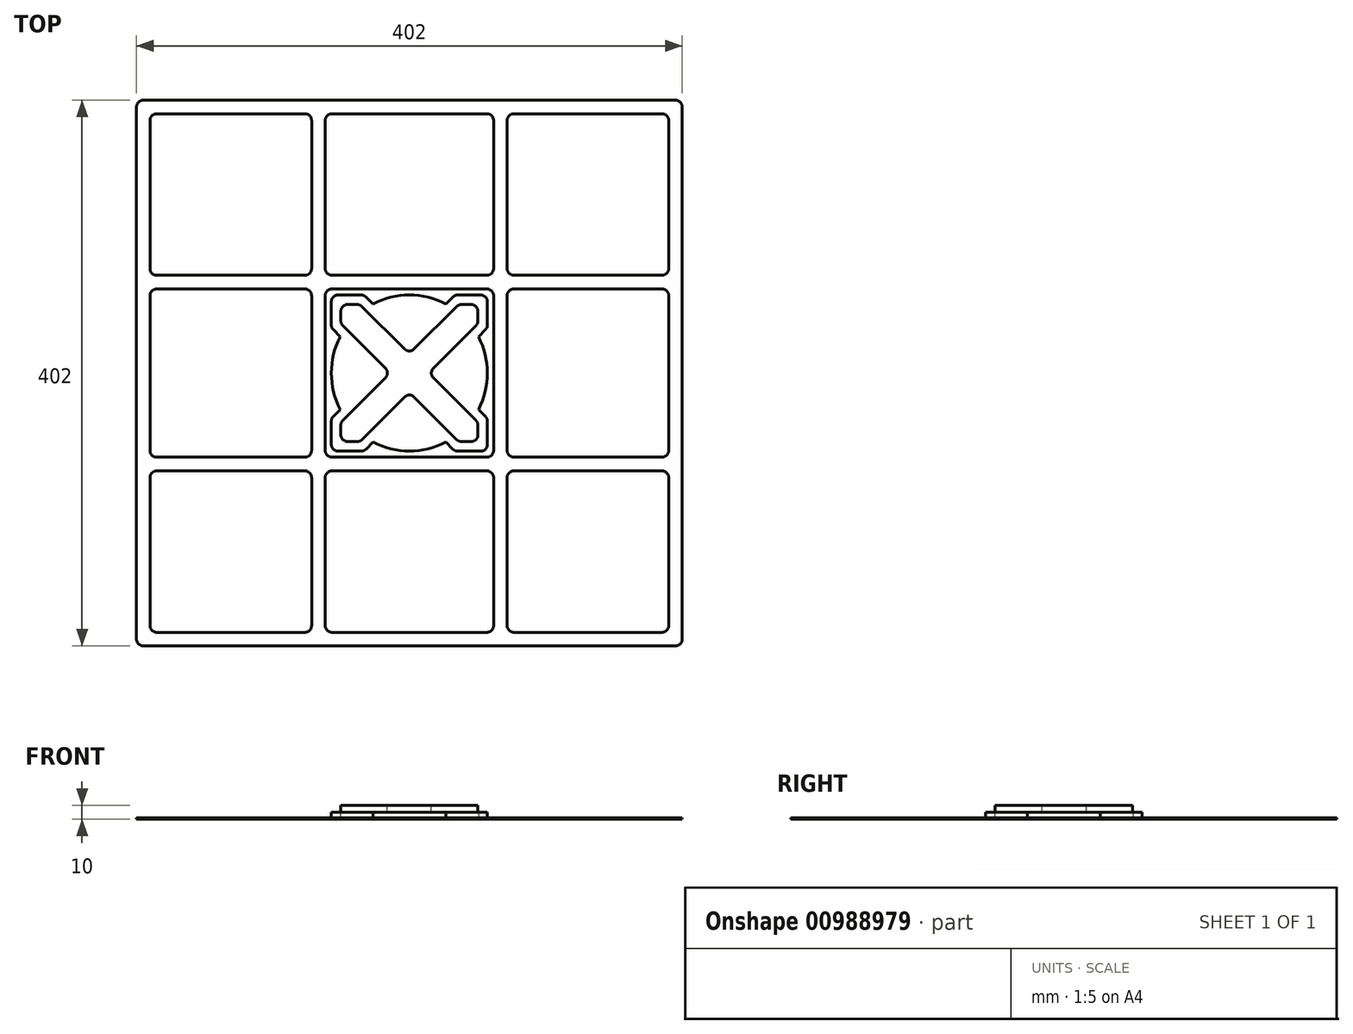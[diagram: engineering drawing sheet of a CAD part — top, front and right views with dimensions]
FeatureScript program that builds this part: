
annotation { "Feature Type Name" : "Feature", "Feature Type Description" : "" }
export const myFeature = defineFeature(function(context is Context, id is Id, definition is map)
    precondition{}
    {
        {
            var Q0;
            Q0=qCreatedBy(makeId("Top.planeOp"),FACE);
            var sketch = newSketch(context, id + "F0", { "sketchPlane" : qUnion([Q0])});
            skLineSegment(sketch, "E0.bottom", {"start": v(57.5, 57.5) * mm, "end": v(-57.5, 57.5) * mm, "construction": true});
            skLineSegment(sketch, "E0.top", {"start": v(57.5, -57.5) * mm, "end": v(-57.5, -57.5) * mm, "construction": true});
            skLineSegment(sketch, "E0.left", {"start": v(57.5, 57.5) * mm, "end": v(57.5, -57.5) * mm, "construction": true});
            skLineSegment(sketch, "E0.right", {"start": v(-57.5, 57.5) * mm, "end": v(-57.5, -57.5) * mm, "construction": true});
            skPoint(sketch, "E0.middle", {"position": v(0, 0) * mm});
            skLineSegment(sketch, "E1", {"start": v(-57.5, 57.5) * mm, "end": v(57.5, -57.5) * mm, "construction": true});
            skLineSegment(sketch, "E2.0", {"start": v(-69.52, 45.48) * mm, "end": v(-24.04, 0) * mm});
            skLineSegment(sketch, "E3.0", {"start": v(-45.48, 69.52) * mm, "end": v(0, 24.04) * mm});
            skLineSegment(sketch, "E4.MirrorCS", {"start": v(45.48, 69.52) * mm, "end": v(0, 24.04) * mm});
            skLineSegment(sketch, "E5.MirrorCS", {"start": v(69.52, 45.48) * mm, "end": v(24.04, 0) * mm});
            skLineSegment(sketch, "E6.trimOffspring", {"start": v(24.04, 0) * mm, "end": v(72.02, -47.98) * mm});
            skLineSegment(sketch, "E7.trimOffspring", {"start": v(-24.04, 0) * mm, "end": v(-72.02, -47.98) * mm});
            skLineSegment(sketch, "E8.trimOffspring", {"start": v(0, -24.04) * mm, "end": v(47.98, -72.02) * mm});
            skLineSegment(sketch, "E9.trimOffspring", {"start": v(0, -24.04) * mm, "end": v(-47.98, -72.02) * mm});
            skLineSegment(sketch, "E10", {"start": v(-57.5, 33.46) * mm, "end": v(-57.5, 57.5) * mm});
            skLineSegment(sketch, "E11", {"start": v(-33.46, 57.5) * mm, "end": v(-57.5, 57.5) * mm});
            skLineSegment(sketch, "E12", {"start": v(33.46, 57.5) * mm, "end": v(57.5, 57.5) * mm});
            skLineSegment(sketch, "E13", {"start": v(57.5, 33.46) * mm, "end": v(57.5, 57.5) * mm});
            skLineSegment(sketch, "E14.MirrorCS", {"start": v(-57.5, -33.46) * mm, "end": v(-57.5, -57.5) * mm});
            skLineSegment(sketch, "E15.MirrorCS", {"start": v(-33.46, -57.5) * mm, "end": v(-57.5, -57.5) * mm});
            skLineSegment(sketch, "E16.MirrorCS", {"start": v(33.46, -57.5) * mm, "end": v(57.5, -57.5) * mm});
            skLineSegment(sketch, "E17.MirrorCS", {"start": v(57.5, -33.46) * mm, "end": v(57.5, -57.5) * mm});
            skSolve(sketch);
        }
        {
            var Q0;
            {var subQ1=sQuery(id+"F0.wireOp",EDGE,"E10");Q0=makeQuery(id+"F0.imprint","IMPRINT",FACE,{"disambiguationData":[TD([[makeQuery(id+"F0.imprint","IMPRINT",EDGE,{"derivedFrom":subQ1}),-1.0]])]});}
            extrude(context, id + "F1", {"entities" : qUnion([Q0]), "depth" : 5 * mm, "offsetDistance" : 25 * mm});
        }
        {
            var Q0;
            Q0=makeQuery(id+"F1.opExtrude","SWEPT_EDGE",EDGE,{"disambiguationData":[OSD([sQuery(id+"F0.wireOp",EDGE,"E14.MirrorCS"),sQuery(id+"F0.wireOp",EDGE,"E15.MirrorCS")])]});
            var Q1;
            Q1=makeQuery(id+"F1.opExtrude","SWEPT_EDGE",EDGE,{"disambiguationData":[OSD([sQuery(id+"F0.wireOp",EDGE,"E9.trimOffspring"),sQuery(id+"F0.wireOp",EDGE,"E15.MirrorCS")])]});
            var Q2;
            Q2=makeQuery(id+"F1.opExtrude","SWEPT_EDGE",EDGE,{"disambiguationData":[OSD([sQuery(id+"F0.wireOp",EDGE,"E8.trimOffspring"),sQuery(id+"F0.wireOp",EDGE,"E16.MirrorCS")])]});
            var Q3;
            Q3=makeQuery(id+"F1.opExtrude","SWEPT_EDGE",EDGE,{"disambiguationData":[OSD([sQuery(id+"F0.wireOp",EDGE,"E8.trimOffspring"),sQuery(id+"F0.wireOp",EDGE,"E9.trimOffspring")])]});
            var Q4;
            Q4=makeQuery(id+"F1.opExtrude","SWEPT_EDGE",EDGE,{"disambiguationData":[OSD([sQuery(id+"F0.wireOp",EDGE,"E16.MirrorCS"),sQuery(id+"F0.wireOp",EDGE,"E17.MirrorCS")])]});
            var Q5;
            Q5=makeQuery(id+"F1.opExtrude","SWEPT_EDGE",EDGE,{"disambiguationData":[OSD([sQuery(id+"F0.wireOp",EDGE,"E6.trimOffspring"),sQuery(id+"F0.wireOp",EDGE,"E17.MirrorCS")])]});
            var Q6;
            Q6=makeQuery(id+"F1.opExtrude","SWEPT_EDGE",EDGE,{"disambiguationData":[OSD([sQuery(id+"F0.wireOp",EDGE,"E5.MirrorCS"),sQuery(id+"F0.wireOp",EDGE,"E6.trimOffspring")])]});
            var Q7;
            Q7=makeQuery(id+"F1.opExtrude","SWEPT_EDGE",EDGE,{"disambiguationData":[OSD([sQuery(id+"F0.wireOp",EDGE,"E5.MirrorCS"),sQuery(id+"F0.wireOp",EDGE,"E13")])]});
            var Q8;
            Q8=makeQuery(id+"F1.opExtrude","SWEPT_EDGE",EDGE,{"disambiguationData":[OSD([sQuery(id+"F0.wireOp",EDGE,"E12"),sQuery(id+"F0.wireOp",EDGE,"E13")])]});
            var Q9;
            Q9=makeQuery(id+"F1.opExtrude","SWEPT_EDGE",EDGE,{"disambiguationData":[OSD([sQuery(id+"F0.wireOp",EDGE,"E4.MirrorCS"),sQuery(id+"F0.wireOp",EDGE,"E12")])]});
            var Q10;
            Q10=makeQuery(id+"F1.opExtrude","SWEPT_EDGE",EDGE,{"disambiguationData":[OSD([sQuery(id+"F0.wireOp",EDGE,"E3.0"),sQuery(id+"F0.wireOp",EDGE,"E4.MirrorCS")])]});
            var Q11;
            Q11=makeQuery(id+"F1.opExtrude","SWEPT_EDGE",EDGE,{"disambiguationData":[OSD([sQuery(id+"F0.wireOp",EDGE,"E3.0"),sQuery(id+"F0.wireOp",EDGE,"E11")])]});
            var Q12;
            Q12=makeQuery(id+"F1.opExtrude","SWEPT_EDGE",EDGE,{"disambiguationData":[OSD([sQuery(id+"F0.wireOp",EDGE,"E10"),sQuery(id+"F0.wireOp",EDGE,"E11")])]});
            var Q13;
            Q13=makeQuery(id+"F1.opExtrude","SWEPT_EDGE",EDGE,{"disambiguationData":[OSD([sQuery(id+"F0.wireOp",EDGE,"E2.0"),sQuery(id+"F0.wireOp",EDGE,"E10")])]});
            var Q14;
            Q14=makeQuery(id+"F1.opExtrude","SWEPT_EDGE",EDGE,{"disambiguationData":[OSD([sQuery(id+"F0.wireOp",EDGE,"E2.0"),sQuery(id+"F0.wireOp",EDGE,"E7.trimOffspring")])]});
            var Q15;
            Q15=makeQuery(id+"F1.opExtrude","SWEPT_EDGE",EDGE,{"disambiguationData":[OSD([sQuery(id+"F0.wireOp",EDGE,"E7.trimOffspring"),sQuery(id+"F0.wireOp",EDGE,"E14.MirrorCS")])]});
            fillet(context, id + "F2", {"entities" : qUnion([Q0, Q1, Q2, Q3, Q4, Q5, Q6, Q7, Q8, Q9, Q10, Q11, Q12, Q13, Q14, Q15]), "radius" : 5 * mm, "tangentPropagation" : true, "allowEdgeOverflow" : false});
        }
        {
            var Q0;
            Q0=qCreatedBy(makeId("Top.planeOp"),FACE);
            var sketch = newSketch(context, id + "F3", { "sketchPlane" : qUnion([Q0])});
            skLineSegment(sketch, "E18.bottom", {"start": v(-57.5, 57.5) * mm, "end": v(57.5, 57.5) * mm, "construction": true});
            skLineSegment(sketch, "E18.top", {"start": v(-57.5, -57.5) * mm, "end": v(57.5, -57.5) * mm, "construction": true});
            skLineSegment(sketch, "E18.left", {"start": v(-57.5, 57.5) * mm, "end": v(-57.5, -57.5) * mm, "construction": true});
            skLineSegment(sketch, "E18.right", {"start": v(57.5, 57.5) * mm, "end": v(57.5, -57.5) * mm, "construction": true});
            skPoint(sketch, "E18.middle", {"position": v(0, 0) * mm});
            skCircle(sketch, "E19", {"center": v(0, 0) * mm, "radius": 57.5 * mm});
            skCircle(sketch, "E20.0", {"center": v(0, 0) * mm, "radius": 22.5 * mm});
            skSolve(sketch);
        }
        {
            var Q0;
            Q0=makeQuery(id+"F3.imprint","IMPRINT",FACE,{"disambiguationData":[TD([[makeQuery(id+"F3.imprint","IMPRINT",EDGE,{"derivedFrom":sQuery(id+"F3.wireOp",EDGE,"E19")}),1.0]])]});
            extrude(context, id + "F4", {"entities" : qUnion([Q0]), "depth" : 5 * mm, "offsetDistance" : 25 * mm});
        }
        {
            var Q0;
            Q0=qCreatedBy(makeId("Top.planeOp"),FACE);
            var sketch = newSketch(context, id + "F5", { "sketchPlane" : qUnion([Q0])});
            skLineSegment(sketch, "E21.bottom", {"start": v(201, 201) * mm, "end": v(-201, 201) * mm});
            skLineSegment(sketch, "E21.top", {"start": v(201, -201) * mm, "end": v(-201, -201) * mm});
            skLineSegment(sketch, "E21.left", {"start": v(201, 201) * mm, "end": v(201, -201) * mm});
            skLineSegment(sketch, "E21.right", {"start": v(-201, 201) * mm, "end": v(-201, -201) * mm});
            skPoint(sketch, "E21.middle", {"position": v(0, 0) * mm});
            skLineSegment(sketch, "E22", {"start": v(-67, 201) * mm, "end": v(-67, -201) * mm, "construction": true});
            skLineSegment(sketch, "E23", {"start": v(201, 67) * mm, "end": v(-201, 67) * mm, "construction": true});
            skLineSegment(sketch, "E24.MirrorCS", {"start": v(67, 201) * mm, "end": v(67, -201) * mm, "construction": true});
            skLineSegment(sketch, "E25.MirrorCS", {"start": v(201, -67) * mm, "end": v(-201, -67) * mm, "construction": true});
            skLineSegment(sketch, "E26.0", {"start": v(-191, 191) * mm, "end": v(-191, 72) * mm});
            skLineSegment(sketch, "E26.1", {"start": v(191, 191) * mm, "end": v(72, 191) * mm});
            skLineSegment(sketch, "E26.2", {"start": v(191, 191) * mm, "end": v(191, 72) * mm});
            skLineSegment(sketch, "E26.3", {"start": v(191, -191) * mm, "end": v(72, -191) * mm});
            skLineSegment(sketch, "E27.0", {"start": v(-72, 191) * mm, "end": v(-72, 72) * mm});
            skLineSegment(sketch, "E28.0", {"start": v(-62, 191) * mm, "end": v(-62, 72) * mm});
            skLineSegment(sketch, "E29.0", {"start": v(191, 72) * mm, "end": v(72, 72) * mm});
            skLineSegment(sketch, "E30.0", {"start": v(191, 62) * mm, "end": v(72, 62) * mm});
            skLineSegment(sketch, "E31.0", {"start": v(62, 191) * mm, "end": v(62, 72) * mm});
            skLineSegment(sketch, "E32.0", {"start": v(72, 191) * mm, "end": v(72, 72) * mm});
            skLineSegment(sketch, "E33.0", {"start": v(191, -62) * mm, "end": v(72, -62) * mm});
            skLineSegment(sketch, "E34.0", {"start": v(191, -72) * mm, "end": v(72, -72) * mm});
            skLineSegment(sketch, "E35.trimOffspring", {"start": v(-191, 62) * mm, "end": v(-191, -62) * mm});
            skLineSegment(sketch, "E36.trimOffspring", {"start": v(-72, 72) * mm, "end": v(-191, 72) * mm});
            skLineSegment(sketch, "E37.trimOffspring", {"start": v(-72, 62) * mm, "end": v(-72, -62) * mm});
            skLineSegment(sketch, "E38.trimOffspring", {"start": v(-72, 62) * mm, "end": v(-191, 62) * mm});
            skLineSegment(sketch, "E39.trimOffspring", {"start": v(-62, 62) * mm, "end": v(-62, -62) * mm});
            skLineSegment(sketch, "E40.trimOffspring", {"start": v(62, 62) * mm, "end": v(62, -62) * mm});
            skLineSegment(sketch, "E41.trimOffspring", {"start": v(62, 72) * mm, "end": v(-62, 72) * mm});
            skLineSegment(sketch, "E42.trimOffspring", {"start": v(72, 62) * mm, "end": v(72, -62) * mm});
            skLineSegment(sketch, "E43.trimOffspring", {"start": v(62, 62) * mm, "end": v(-62, 62) * mm});
            skLineSegment(sketch, "E44.trimOffspring", {"start": v(191, 62) * mm, "end": v(191, -62) * mm});
            skLineSegment(sketch, "E45.trimOffspring", {"start": v(191, -72) * mm, "end": v(191, -191) * mm});
            skLineSegment(sketch, "E46.trimOffspring", {"start": v(62, -72) * mm, "end": v(62, -191) * mm});
            skLineSegment(sketch, "E47.trimOffspring", {"start": v(62, -72) * mm, "end": v(-62, -72) * mm});
            skLineSegment(sketch, "E48.trimOffspring", {"start": v(72, -72) * mm, "end": v(72, -191) * mm});
            skLineSegment(sketch, "E49.trimOffspring", {"start": v(62, -62) * mm, "end": v(-62, -62) * mm});
            skLineSegment(sketch, "E50.trimOffspring", {"start": v(-72, -62) * mm, "end": v(-191, -62) * mm});
            skLineSegment(sketch, "E51.trimOffspring", {"start": v(-72, -72) * mm, "end": v(-72, -191) * mm});
            skLineSegment(sketch, "E52.trimOffspring", {"start": v(-72, -72) * mm, "end": v(-191, -72) * mm});
            skLineSegment(sketch, "E53.trimOffspring", {"start": v(-62, -72) * mm, "end": v(-62, -191) * mm});
            skLineSegment(sketch, "E54.trimOffspring", {"start": v(-72, -191) * mm, "end": v(-191, -191) * mm});
            skLineSegment(sketch, "E55.trimOffspring", {"start": v(62, -191) * mm, "end": v(-62, -191) * mm});
            skLineSegment(sketch, "E56.trimOffspring", {"start": v(-191, -72) * mm, "end": v(-191, -191) * mm});
            skLineSegment(sketch, "E57.trimOffspring", {"start": v(62, 191) * mm, "end": v(-62, 191) * mm});
            skLineSegment(sketch, "E58.trimOffspring", {"start": v(-72, 191) * mm, "end": v(-191, 191) * mm});
            skSolve(sketch);
        }
        {
            var Q0;
            Q0=makeQuery(id+"F5.imprint","IMPRINT",FACE,{"disambiguationData":[TD([[makeQuery(id+"F5.imprint","IMPRINT",EDGE,{"derivedFrom":sQuery(id+"F5.wireOp",EDGE,"E21.bottom")}),1.0]])]});
            extrude(context, id + "F6", {"entities" : qUnion([Q0]), "depth" : 1 * mm, "offsetDistance" : 25 * mm});
        }
        {
            var Q0;
            Q0=makeQuery(id+"F5.imprint","IMPRINT",FACE,{"disambiguationData":[TD([[makeQuery(id+"F5.imprint","IMPRINT",EDGE,{"derivedFrom":sQuery(id+"F5.wireOp",EDGE,"E26.3")}),-1.0]])]});
            var Q1;
            Q1=makeQuery(id+"F5.imprint","IMPRINT",FACE,{"disambiguationData":[TD([[makeQuery(id+"F5.imprint","IMPRINT",EDGE,{"derivedFrom":sQuery(id+"F5.wireOp",EDGE,"E46.trimOffspring")}),-1.0]])]});
            var Q2;
            Q2=makeQuery(id+"F5.imprint","IMPRINT",FACE,{"disambiguationData":[TD([[makeQuery(id+"F5.imprint","IMPRINT",EDGE,{"derivedFrom":sQuery(id+"F5.wireOp",EDGE,"E30.0")}),1.0]])]});
            var Q3;
            Q3=makeQuery(id+"F5.imprint","IMPRINT",FACE,{"disambiguationData":[TD([[makeQuery(id+"F5.imprint","IMPRINT",EDGE,{"derivedFrom":sQuery(id+"F5.wireOp",EDGE,"E51.trimOffspring")}),-1.0]])]});
            var Q4;
            Q4=makeQuery(id+"F5.imprint","IMPRINT",FACE,{"disambiguationData":[TD([[makeQuery(id+"F5.imprint","IMPRINT",EDGE,{"derivedFrom":sQuery(id+"F5.wireOp",EDGE,"E21.bottom")}),1.0]])]});
            var Q5;
            Q5=makeQuery(id+"F5.imprint","IMPRINT",FACE,{"disambiguationData":[TD([[makeQuery(id+"F5.imprint","IMPRINT",EDGE,{"derivedFrom":sQuery(id+"F5.wireOp",EDGE,"E39.trimOffspring")}),1.0]])]});
            var Q6;
            Q6=makeQuery(id+"F5.imprint","IMPRINT",FACE,{"disambiguationData":[TD([[makeQuery(id+"F5.imprint","IMPRINT",EDGE,{"derivedFrom":sQuery(id+"F5.wireOp",EDGE,"E26.0")}),1.0]])]});
            var Q7;
            Q7=makeQuery(id+"F5.imprint","IMPRINT",FACE,{"disambiguationData":[TD([[makeQuery(id+"F5.imprint","IMPRINT",EDGE,{"derivedFrom":sQuery(id+"F5.wireOp",EDGE,"E26.1")}),1.0]])]});
            var Q8;
            Q8=makeQuery(id+"F5.imprint","IMPRINT",FACE,{"disambiguationData":[TD([[makeQuery(id+"F5.imprint","IMPRINT",EDGE,{"derivedFrom":sQuery(id+"F5.wireOp",EDGE,"E35.trimOffspring")}),1.0]])]});
            var Q9;
            Q9=makeQuery(id+"F5.imprint","IMPRINT",FACE,{"disambiguationData":[TD([[makeQuery(id+"F5.imprint","IMPRINT",EDGE,{"derivedFrom":sQuery(id+"F5.wireOp",EDGE,"E28.0")}),1.0]])]});
            extrude(context, id + "F7", {"entities" : qUnion([Q0, Q1, Q2, Q3, Q4, Q5, Q6, Q7, Q8, Q9]), "operationType" : NewBodyOperationType.ADD, "depth" : 0.5 * mm, "offsetDistance" : 25 * mm});
        }
        {
            var Q0;
            Q0=makeQuery(id+"F6.opExtrude","SWEPT_EDGE",EDGE,{"disambiguationData":[OSD([sQuery(id+"F5.wireOp",EDGE,"E31.0"),sQuery(id+"F5.wireOp",EDGE,"E57.trimOffspring")])]});
            var Q1;
            Q1=makeQuery(id+"F6.opExtrude","SWEPT_EDGE",EDGE,{"disambiguationData":[OSD([sQuery(id+"F5.wireOp",EDGE,"E26.1"),sQuery(id+"F5.wireOp",EDGE,"E26.2")])]});
            var Q2;
            Q2=makeQuery(id+"F6.opExtrude","SWEPT_EDGE",EDGE,{"disambiguationData":[OSD([sQuery(id+"F5.wireOp",EDGE,"E27.0"),sQuery(id+"F5.wireOp",EDGE,"E58.trimOffspring")])]});
            var Q3;
            Q3=makeQuery(id+"F6.opExtrude","SWEPT_EDGE",EDGE,{"disambiguationData":[OSD([sQuery(id+"F5.wireOp",EDGE,"E37.trimOffspring"),sQuery(id+"F5.wireOp",EDGE,"E38.trimOffspring")])]});
            var Q4;
            Q4=makeQuery(id+"F6.opExtrude","SWEPT_EDGE",EDGE,{"disambiguationData":[OSD([sQuery(id+"F5.wireOp",EDGE,"E40.trimOffspring"),sQuery(id+"F5.wireOp",EDGE,"E43.trimOffspring")])]});
            var Q5;
            Q5=makeQuery(id+"F6.opExtrude","SWEPT_EDGE",EDGE,{"disambiguationData":[OSD([sQuery(id+"F5.wireOp",EDGE,"E30.0"),sQuery(id+"F5.wireOp",EDGE,"E44.trimOffspring")])]});
            var Q6;
            Q6=makeQuery(id+"F6.opExtrude","SWEPT_EDGE",EDGE,{"disambiguationData":[OSD([sQuery(id+"F5.wireOp",EDGE,"E34.0"),sQuery(id+"F5.wireOp",EDGE,"E45.trimOffspring")])]});
            var Q7;
            Q7=makeQuery(id+"F6.opExtrude","SWEPT_EDGE",EDGE,{"disambiguationData":[OSD([sQuery(id+"F5.wireOp",EDGE,"E46.trimOffspring"),sQuery(id+"F5.wireOp",EDGE,"E47.trimOffspring")])]});
            var Q8;
            Q8=makeQuery(id+"F6.opExtrude","SWEPT_EDGE",EDGE,{"disambiguationData":[OSD([sQuery(id+"F5.wireOp",EDGE,"E51.trimOffspring"),sQuery(id+"F5.wireOp",EDGE,"E52.trimOffspring")])]});
            var Q9;
            Q9=makeQuery(id+"F6.opExtrude","SWEPT_EDGE",EDGE,{"disambiguationData":[OSD([sQuery(id+"F5.wireOp",EDGE,"E26.3"),sQuery(id+"F5.wireOp",EDGE,"E45.trimOffspring")])]});
            var Q10;
            Q10=makeQuery(id+"F6.opExtrude","SWEPT_EDGE",EDGE,{"disambiguationData":[OSD([sQuery(id+"F5.wireOp",EDGE,"E33.0"),sQuery(id+"F5.wireOp",EDGE,"E44.trimOffspring")])]});
            var Q11;
            Q11=makeQuery(id+"F6.opExtrude","SWEPT_EDGE",EDGE,{"disambiguationData":[OSD([sQuery(id+"F5.wireOp",EDGE,"E26.2"),sQuery(id+"F5.wireOp",EDGE,"E29.0")])]});
            var Q12;
            Q12=makeQuery(id+"F6.opExtrude","SWEPT_EDGE",EDGE,{"disambiguationData":[OSD([sQuery(id+"F5.wireOp",EDGE,"E31.0"),sQuery(id+"F5.wireOp",EDGE,"E41.trimOffspring")])]});
            var Q13;
            Q13=makeQuery(id+"F6.opExtrude","SWEPT_EDGE",EDGE,{"disambiguationData":[OSD([sQuery(id+"F5.wireOp",EDGE,"E40.trimOffspring"),sQuery(id+"F5.wireOp",EDGE,"E49.trimOffspring")])]});
            var Q14;
            Q14=makeQuery(id+"F6.opExtrude","SWEPT_EDGE",EDGE,{"disambiguationData":[OSD([sQuery(id+"F5.wireOp",EDGE,"E46.trimOffspring"),sQuery(id+"F5.wireOp",EDGE,"E55.trimOffspring")])]});
            var Q15;
            Q15=makeQuery(id+"F6.opExtrude","SWEPT_EDGE",EDGE,{"disambiguationData":[OSD([sQuery(id+"F5.wireOp",EDGE,"E51.trimOffspring"),sQuery(id+"F5.wireOp",EDGE,"E54.trimOffspring")])]});
            var Q16;
            Q16=makeQuery(id+"F6.opExtrude","SWEPT_EDGE",EDGE,{"disambiguationData":[OSD([sQuery(id+"F5.wireOp",EDGE,"E37.trimOffspring"),sQuery(id+"F5.wireOp",EDGE,"E50.trimOffspring")])]});
            var Q17;
            Q17=makeQuery(id+"F6.opExtrude","SWEPT_EDGE",EDGE,{"disambiguationData":[OSD([sQuery(id+"F5.wireOp",EDGE,"E27.0"),sQuery(id+"F5.wireOp",EDGE,"E36.trimOffspring")])]});
            var Q18;
            Q18=makeQuery(id+"F6.opExtrude","SWEPT_EDGE",EDGE,{"disambiguationData":[OSD([sQuery(id+"F5.wireOp",EDGE,"E26.3"),sQuery(id+"F5.wireOp",EDGE,"E48.trimOffspring")])]});
            var Q19;
            Q19=makeQuery(id+"F6.opExtrude","SWEPT_EDGE",EDGE,{"disambiguationData":[OSD([sQuery(id+"F5.wireOp",EDGE,"E53.trimOffspring"),sQuery(id+"F5.wireOp",EDGE,"E55.trimOffspring")])]});
            var Q20;
            Q20=makeQuery(id+"F6.opExtrude","SWEPT_EDGE",EDGE,{"disambiguationData":[OSD([sQuery(id+"F5.wireOp",EDGE,"E54.trimOffspring"),sQuery(id+"F5.wireOp",EDGE,"E56.trimOffspring")])]});
            var Q21;
            Q21=makeQuery(id+"F6.opExtrude","SWEPT_EDGE",EDGE,{"disambiguationData":[OSD([sQuery(id+"F5.wireOp",EDGE,"E35.trimOffspring"),sQuery(id+"F5.wireOp",EDGE,"E50.trimOffspring")])]});
            var Q22;
            Q22=makeQuery(id+"F6.opExtrude","SWEPT_EDGE",EDGE,{"disambiguationData":[OSD([sQuery(id+"F5.wireOp",EDGE,"E39.trimOffspring"),sQuery(id+"F5.wireOp",EDGE,"E49.trimOffspring")])]});
            var Q23;
            Q23=makeQuery(id+"F6.opExtrude","SWEPT_EDGE",EDGE,{"disambiguationData":[OSD([sQuery(id+"F5.wireOp",EDGE,"E33.0"),sQuery(id+"F5.wireOp",EDGE,"E42.trimOffspring")])]});
            var Q24;
            Q24=makeQuery(id+"F6.opExtrude","SWEPT_EDGE",EDGE,{"disambiguationData":[OSD([sQuery(id+"F5.wireOp",EDGE,"E29.0"),sQuery(id+"F5.wireOp",EDGE,"E32.0")])]});
            var Q25;
            Q25=makeQuery(id+"F6.opExtrude","SWEPT_EDGE",EDGE,{"disambiguationData":[OSD([sQuery(id+"F5.wireOp",EDGE,"E28.0"),sQuery(id+"F5.wireOp",EDGE,"E41.trimOffspring")])]});
            var Q26;
            Q26=makeQuery(id+"F6.opExtrude","SWEPT_EDGE",EDGE,{"disambiguationData":[OSD([sQuery(id+"F5.wireOp",EDGE,"E26.0"),sQuery(id+"F5.wireOp",EDGE,"E36.trimOffspring")])]});
            var Q27;
            Q27=makeQuery(id+"F6.opExtrude","SWEPT_EDGE",EDGE,{"disambiguationData":[OSD([sQuery(id+"F5.wireOp",EDGE,"E26.0"),sQuery(id+"F5.wireOp",EDGE,"E58.trimOffspring")])]});
            var Q28;
            Q28=makeQuery(id+"F6.opExtrude","SWEPT_EDGE",EDGE,{"disambiguationData":[OSD([sQuery(id+"F5.wireOp",EDGE,"E28.0"),sQuery(id+"F5.wireOp",EDGE,"E57.trimOffspring")])]});
            var Q29;
            Q29=makeQuery(id+"F6.opExtrude","SWEPT_EDGE",EDGE,{"disambiguationData":[OSD([sQuery(id+"F5.wireOp",EDGE,"E26.1"),sQuery(id+"F5.wireOp",EDGE,"E32.0")])]});
            var Q30;
            Q30=makeQuery(id+"F6.opExtrude","SWEPT_EDGE",EDGE,{"disambiguationData":[OSD([sQuery(id+"F5.wireOp",EDGE,"E30.0"),sQuery(id+"F5.wireOp",EDGE,"E42.trimOffspring")])]});
            var Q31;
            Q31=makeQuery(id+"F6.opExtrude","SWEPT_EDGE",EDGE,{"disambiguationData":[OSD([sQuery(id+"F5.wireOp",EDGE,"E39.trimOffspring"),sQuery(id+"F5.wireOp",EDGE,"E43.trimOffspring")])]});
            var Q32;
            Q32=makeQuery(id+"F6.opExtrude","SWEPT_EDGE",EDGE,{"disambiguationData":[OSD([sQuery(id+"F5.wireOp",EDGE,"E35.trimOffspring"),sQuery(id+"F5.wireOp",EDGE,"E38.trimOffspring")])]});
            var Q33;
            Q33=makeQuery(id+"F6.opExtrude","SWEPT_EDGE",EDGE,{"disambiguationData":[OSD([sQuery(id+"F5.wireOp",EDGE,"E52.trimOffspring"),sQuery(id+"F5.wireOp",EDGE,"E56.trimOffspring")])]});
            var Q34;
            Q34=makeQuery(id+"F6.opExtrude","SWEPT_EDGE",EDGE,{"disambiguationData":[OSD([sQuery(id+"F5.wireOp",EDGE,"E47.trimOffspring"),sQuery(id+"F5.wireOp",EDGE,"E53.trimOffspring")])]});
            var Q35;
            Q35=makeQuery(id+"F6.opExtrude","SWEPT_EDGE",EDGE,{"disambiguationData":[OSD([sQuery(id+"F5.wireOp",EDGE,"E34.0"),sQuery(id+"F5.wireOp",EDGE,"E48.trimOffspring")])]});
            fillet(context, id + "F8", {"entities" : qUnion([Q0, Q1, Q2, Q3, Q4, Q5, Q6, Q7, Q8, Q9, Q10, Q11, Q12, Q13, Q14, Q15, Q16, Q17, Q18, Q19, Q20, Q21, Q22, Q23, Q24, Q25, Q26, Q27, Q28, Q29, Q30, Q31, Q32, Q33, Q34, Q35]), "radius" : 5 * mm, "tangentPropagation" : true, "allowEdgeOverflow" : false});
        }
        {
            var Q0;
            Q0=makeQuery(id+"F6.opExtrude","SWEPT_EDGE",EDGE,{"disambiguationData":[OSD([sQuery(id+"F5.wireOp",EDGE,"E21.top"),sQuery(id+"F5.wireOp",EDGE,"E21.right")])]});
            var Q1;
            Q1=makeQuery(id+"F6.opExtrude","SWEPT_EDGE",EDGE,{"disambiguationData":[OSD([sQuery(id+"F5.wireOp",EDGE,"E21.bottom"),sQuery(id+"F5.wireOp",EDGE,"E21.right")])]});
            var Q2;
            Q2=makeQuery(id+"F6.opExtrude","SWEPT_EDGE",EDGE,{"disambiguationData":[OSD([sQuery(id+"F5.wireOp",EDGE,"E21.bottom"),sQuery(id+"F5.wireOp",EDGE,"E21.left")])]});
            var Q3;
            Q3=makeQuery(id+"F6.opExtrude","SWEPT_EDGE",EDGE,{"disambiguationData":[OSD([sQuery(id+"F5.wireOp",EDGE,"E21.top"),sQuery(id+"F5.wireOp",EDGE,"E21.left")])]});
            fillet(context, id + "F9", {"entities" : qUnion([Q0, Q1, Q2, Q3]), "radius" : 5 * mm, "tangentPropagation" : true, "allowEdgeOverflow" : false});
        }
        {
            var Q0;
            Q0=makeQuery(id+"F1.opExtrude","CAP_FACE",FACE,{"disambiguationData":[OSD([sQuery(id+"F0.wireOp",EDGE,"E2.0"),sQuery(id+"F0.wireOp",EDGE,"E3.0"),sQuery(id+"F0.wireOp",EDGE,"E4.MirrorCS"),sQuery(id+"F0.wireOp",EDGE,"E5.MirrorCS"),sQuery(id+"F0.wireOp",EDGE,"E6.trimOffspring"),sQuery(id+"F0.wireOp",EDGE,"E7.trimOffspring"),sQuery(id+"F0.wireOp",EDGE,"E8.trimOffspring"),sQuery(id+"F0.wireOp",EDGE,"E9.trimOffspring"),sQuery(id+"F0.wireOp",EDGE,"E10"),sQuery(id+"F0.wireOp",EDGE,"E11"),sQuery(id+"F0.wireOp",EDGE,"E12"),sQuery(id+"F0.wireOp",EDGE,"E13"),sQuery(id+"F0.wireOp",EDGE,"E14.MirrorCS"),sQuery(id+"F0.wireOp",EDGE,"E15.MirrorCS"),sQuery(id+"F0.wireOp",EDGE,"E16.MirrorCS"),sQuery(id+"F0.wireOp",EDGE,"E17.MirrorCS")])],"isStart":false});
            var sketch = newSketch(context, id + "F10", { "sketchPlane" : qUnion([Q0])});
            skLineSegment(sketch, "E59.0", {"start": v(-36.94, 51.09) * mm, "end": v(0, 14.14) * mm});
            skLineSegment(sketch, "E60.0", {"start": v(-51.09, 36.94) * mm, "end": v(-22.63, 8.49) * mm});
            skLineSegment(sketch, "E61.0", {"start": v(-35.53, 50.5) * mm, "end": v(-52.5, 50.5) * mm});
            skLineSegment(sketch, "E62.0", {"start": v(-50.5, 35.53) * mm, "end": v(-50.5, 52.5) * mm});
            skLineSegment(sketch, "E63.MirrorCS", {"start": v(50.5, 35.53) * mm, "end": v(50.5, 52.5) * mm});
            skLineSegment(sketch, "E64.MirrorCS", {"start": v(36.94, 51.09) * mm, "end": v(0, 14.14) * mm});
            skLineSegment(sketch, "E65.MirrorCS", {"start": v(51.09, 36.94) * mm, "end": v(22.63, 8.49) * mm});
            skLineSegment(sketch, "E66.MirrorCS", {"start": v(35.53, 50.5) * mm, "end": v(52.5, 50.5) * mm});
            skLineSegment(sketch, "E67.MirrorCS", {"start": v(-51.09, -36.94) * mm, "end": v(-22.63, -8.49) * mm});
            skLineSegment(sketch, "E68.MirrorCS", {"start": v(36.94, -51.09) * mm, "end": v(0, -14.14) * mm});
            skLineSegment(sketch, "E69.MirrorCS", {"start": v(35.53, -50.5) * mm, "end": v(52.5, -50.5) * mm});
            skLineSegment(sketch, "E70.MirrorCS", {"start": v(-36.94, -51.09) * mm, "end": v(0, -14.14) * mm});
            skLineSegment(sketch, "E71.MirrorCS", {"start": v(50.5, -35.53) * mm, "end": v(50.5, -52.5) * mm});
            skLineSegment(sketch, "E72.MirrorCS", {"start": v(-50.5, -35.53) * mm, "end": v(-50.5, -52.5) * mm});
            skLineSegment(sketch, "E73.MirrorCS", {"start": v(51.09, -36.94) * mm, "end": v(22.63, -8.49) * mm});
            skLineSegment(sketch, "E74.MirrorCS", {"start": v(-35.53, -50.5) * mm, "end": v(-52.5, -50.5) * mm});
            skLineSegment(sketch, "E75.trimOffspring", {"start": v(14.14, 0) * mm, "end": v(22.63, -8.49) * mm});
            skLineSegment(sketch, "E76.trimOffspring", {"start": v(-14.14, 0) * mm, "end": v(-22.63, -8.49) * mm});
            skLineSegment(sketch, "E77.trimOffspring", {"start": v(-14.14, 0) * mm, "end": v(-22.63, 8.49) * mm});
            skLineSegment(sketch, "E78.trimOffspring", {"start": v(14.14, 0) * mm, "end": v(22.63, 8.49) * mm});
            skSolve(sketch);
        }
        {
            var Q0;
            {var subQ33=sQuery(id+"F10.wireOp",EDGE,"E75.trimOffspring");Q0=makeQuery(id+"F10.imprint","IMPRINT",FACE,{"disambiguationData":[TD([[makeQuery(id+"F10.imprint","IMPRINT",EDGE,{"derivedFrom":subQ33}),-1.0]])]});}
            extrude(context, id + "F11", {"entities" : qUnion([Q0]), "operationType" : NewBodyOperationType.ADD, "depth" : 5 * mm, "offsetDistance" : 25 * mm});
        }
        {
            var Q0;
            Q0=makeQuery(id+"F11.opExtrude","SWEPT_EDGE",EDGE,{"disambiguationData":[OSD([sQuery(id+"F10.wireOp",EDGE,"E72.MirrorCS"),sQuery(id+"F10.wireOp",EDGE,"E74.MirrorCS")])]});
            var Q1;
            Q1=makeQuery(id+"F11.opExtrude","SWEPT_EDGE",EDGE,{"disambiguationData":[OSD([sQuery(id+"F10.wireOp",EDGE,"E70.MirrorCS"),sQuery(id+"F10.wireOp",EDGE,"E74.MirrorCS")])]});
            var Q2;
            Q2=makeQuery(id+"F11.opExtrude","SWEPT_EDGE",EDGE,{"disambiguationData":[OSD([sQuery(id+"F10.wireOp",EDGE,"E67.MirrorCS"),sQuery(id+"F10.wireOp",EDGE,"E72.MirrorCS")])]});
            var Q3;
            Q3=makeQuery(id+"F11.opExtrude","SWEPT_EDGE",EDGE,{"disambiguationData":[OSD([sQuery(id+"F10.wireOp",EDGE,"P5LearcC-B3T6-M3SN-7pGu-blPnfo7SSdRu"),sQuery(id+"F10.wireOp",EDGE,"6153ce4e-b949-4285-84fd-3a4493f5ffb4.trimOffspring")])]});
            var Q4;
            Q4=makeQuery(id+"F11.opExtrude","SWEPT_EDGE",EDGE,{"disambiguationData":[OSD([sQuery(id+"F10.wireOp",EDGE,"E68.MirrorCS"),sQuery(id+"F10.wireOp",EDGE,"E69.MirrorCS")])]});
            var Q5;
            Q5=makeQuery(id+"F11.opExtrude","SWEPT_EDGE",EDGE,{"disambiguationData":[OSD([sQuery(id+"F10.wireOp",EDGE,"E69.MirrorCS"),sQuery(id+"F10.wireOp",EDGE,"E71.MirrorCS")])]});
            var Q6;
            Q6=makeQuery(id+"F11.opExtrude","SWEPT_EDGE",EDGE,{"disambiguationData":[OSD([sQuery(id+"F10.wireOp",EDGE,"E71.MirrorCS"),sQuery(id+"F10.wireOp",EDGE,"E73.MirrorCS")])]});
            var Q7;
            Q7=makeQuery(id+"F11.opExtrude","SWEPT_EDGE",EDGE,{"disambiguationData":[OSD([sQuery(id+"F10.wireOp",EDGE,"40ce67f3-5a0b-4920-b6f6-2fed9a026a0d.trimOffspring"),sQuery(id+"F10.wireOp",EDGE,"ac05d8f4-752e-4706-a115-70d05518bb4a.trimOffspring")])]});
            var Q8;
            Q8=makeQuery(id+"F11.opExtrude","SWEPT_EDGE",EDGE,{"disambiguationData":[OSD([sQuery(id+"F10.wireOp",EDGE,"E63.MirrorCS"),sQuery(id+"F10.wireOp",EDGE,"E65.MirrorCS")])]});
            var Q9;
            Q9=makeQuery(id+"F11.opExtrude","SWEPT_EDGE",EDGE,{"disambiguationData":[OSD([sQuery(id+"F10.wireOp",EDGE,"E63.MirrorCS"),sQuery(id+"F10.wireOp",EDGE,"E66.MirrorCS")])]});
            var Q10;
            Q10=makeQuery(id+"F11.opExtrude","SWEPT_EDGE",EDGE,{"disambiguationData":[OSD([sQuery(id+"F10.wireOp",EDGE,"E64.MirrorCS"),sQuery(id+"F10.wireOp",EDGE,"E66.MirrorCS")])]});
            var Q11;
            Q11=makeQuery(id+"F11.opExtrude","SWEPT_EDGE",EDGE,{"disambiguationData":[OSD([sQuery(id+"F10.wireOp",EDGE,"E59.0"),sQuery(id+"F10.wireOp",EDGE,"E61.0")])]});
            var Q12;
            Q12=makeQuery(id+"F11.opExtrude","SWEPT_EDGE",EDGE,{"disambiguationData":[OSD([sQuery(id+"F10.wireOp",EDGE,"E61.0"),sQuery(id+"F10.wireOp",EDGE,"E62.0")])]});
            var Q13;
            Q13=makeQuery(id+"F11.opExtrude","SWEPT_EDGE",EDGE,{"disambiguationData":[OSD([sQuery(id+"F10.wireOp",EDGE,"E60.0"),sQuery(id+"F10.wireOp",EDGE,"E62.0")])]});
            var Q14;
            Q14=makeQuery(id+"F11.opExtrude","SWEPT_EDGE",EDGE,{"disambiguationData":[OSD([sQuery(id+"F10.wireOp",EDGE,"mP6rpeHi-DrQk-PgeI-AXg8-w3PCmxz4PnyT"),sQuery(id+"F10.wireOp",EDGE,"03194a09-976c-451d-88b7-36ccab314b92.trimOffspring")])]});
            var Q15;
            Q15=makeQuery(id+"F11.opExtrude","SWEPT_EDGE",EDGE,{"disambiguationData":[OSD([sQuery(id+"F10.wireOp",EDGE,"5TZM7ayR-7JpK-9xaG-RYf7-GklWVEslqwpp"),sQuery(id+"F10.wireOp",EDGE,"pWoYk1NS-gVno-bRwl-eZRd-lI4ZPA1IjJ0r")])]});
            var Q16;
            Q16=makeQuery(id+"F11.opExtrude","SWEPT_EDGE",EDGE,{"disambiguationData":[OSD([sQuery(id+"F10.wireOp",EDGE,"E68.MirrorCS"),sQuery(id+"F10.wireOp",EDGE,"E70.MirrorCS")])]});
            var Q17;
            Q17=makeQuery(id+"F11.opExtrude","SWEPT_EDGE",EDGE,{"disambiguationData":[OSD([sQuery(id+"F10.wireOp",EDGE,"E76.trimOffspring"),sQuery(id+"F10.wireOp",EDGE,"E77.trimOffspring")])]});
            var Q18;
            Q18=makeQuery(id+"F11.opExtrude","SWEPT_EDGE",EDGE,{"disambiguationData":[OSD([sQuery(id+"F10.wireOp",EDGE,"E59.0"),sQuery(id+"F10.wireOp",EDGE,"E64.MirrorCS")])]});
            var Q19;
            Q19=makeQuery(id+"F11.opExtrude","SWEPT_EDGE",EDGE,{"disambiguationData":[OSD([sQuery(id+"F10.wireOp",EDGE,"E75.trimOffspring"),sQuery(id+"F10.wireOp",EDGE,"E78.trimOffspring")])]});
            fillet(context, id + "F12", {"entities" : qUnion([Q0, Q1, Q2, Q3, Q4, Q5, Q6, Q7, Q8, Q9, Q10, Q11, Q12, Q13, Q14, Q15, Q16, Q17, Q18, Q19]), "radius" : 5 * mm, "tangentPropagation" : true, "allowEdgeOverflow" : false});
        }
    });
